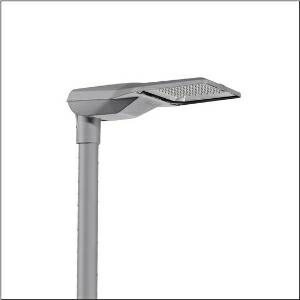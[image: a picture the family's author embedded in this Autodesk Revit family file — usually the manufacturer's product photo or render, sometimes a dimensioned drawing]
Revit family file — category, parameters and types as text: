
# Revit family: streetlight_sl_21_iq_midi___stw1_0a_5xe3e41d08nb_e017
name_source: partatom
category: Lighting Fixtures
units: mm (PartAtom-declared; Revit-internal decimal feet)

## family parameters
Cut with Voids When Loaded = No
Host = Face
Light Source = No
Part Type = Normal
Room Calculation Point = No
Round Connector Dimension = Use Diameter
Shared = No

## types (1)
- --- (1 x LED, 24250 lm, 155.5 W, 4000K)
    Apparent Load = 155 VA
    CIE Flux Codes = 39 75 98 100 100
    Color Rendering = 70
    Color Temperature = 4000K
    Default Elevation = 1800 mm
    Description = Streetlight SL 21 iQ midi, mast luminaire, primary light control with lens, of PMMA, primary optical cover: cover, of toughened safety glass, transparent, light distribution: STW1.0a, light emission: direct distribution, primary light characteristic: asymmetric, installation type: post-top, side-entry, LED, High Power LED, rated luminous flux: 24.250lm, luminous efficacy: 156lm/W, light colour: 740, colour temperature: 4000K, control gear: iQ-Comfort, control: Auto-Match, Temp-Guard, Lumen-Switch, Night-Set, Smart-Wire, Light-Fading, Desk-Remote (wireless, voltage-free reading and setting of iQ features in the workshop via application-optimized NFC function/RFID function), optimised constant luminous flux control (CLO 2.0), pre-setting: linear dimming characteristic, mains connection: 230..240V, AC, 50/60Hz, start of lifetime: 156W, end of service life: 162W, reduction: 69W, luminaire housing, of diecast aluminium, powder-coated, SITECO metallic grey (DB 702S), corrosivity category C5 high according to DIN EN ISO 12944, please order mast flange separately, inclination adjustable: 0°, 5°, 10°, 15°, sealing non-destructively replaceable, multi-level sealing system, length: 644mm, width: 335mm, height: 110mm, mast flange for spigot size: 42mm (side-entry): 5XC10008XM4, 60/48mm (side-entry/post-top): 5XC10108XM2, 76/60mm (side-entry/post-top): 5XC10108XM1, mounting height: 4..8m, protection rating (complete): IP66, insulation class (complete): insulation class II (safety insulation), certification: CE, ENEC, ENEC+, VDE, impact resistance: IK10, permissible operating ambient temperature for outdoor applications: -40..+50°C, standard-compliant lighting for roads and squares, packaging unit: 1 piece

Light Distribution: STW1.0a
    Height = 111 mm
    Lamp = 1 x LED
    Lamp Light Flux = 24250 lm
    Lamp Power = 155.5 W
    Lamp count = 1
    Length = 644 mm
    Luminous efficacy = 156 lm/W
    Manufacturer = Siteco
    ModVariant = No
    Model = 5XE3E41D08NB
    Number of Poles = 1
    OnlyDefault = Yes
    Power Factor = 1
    Product Name = Streetlight SL 21 iQ midi | STW1.0a
    Product group = mast luminaire | pylon top
    ProductGroupID = 6100
    Protection Class = Protection class II
    Protection Degree = IP 66
    RLX_Detail_Level = 1
    RLX_Emergency_Light_Flux = 0 lm
    RLX_Emergency_Type = 0
    RLX_Emergency_Type_DB = No
    RlxData = <blob elided: 27261 chars, md5=124ce91c>
    Socket = socket
    Standby Power = 0 W
    System Light Flux = 24250 lm
    System Power = 155 W
    Type Comments = factory setting: luminous flux: 100 % | dim-lin: 254 | 823 mA
    Type Image = l_1004298.jpg
    URL = http://relux.com
    VarID = @adj_169321
    Voltage = 0 V
    Weight = 0.00 kg
    Width = 336 mm

## geometry (parser evidence)
native form markers: Blend x4, Sweep x11
no freeform markers — native parametric forms only
